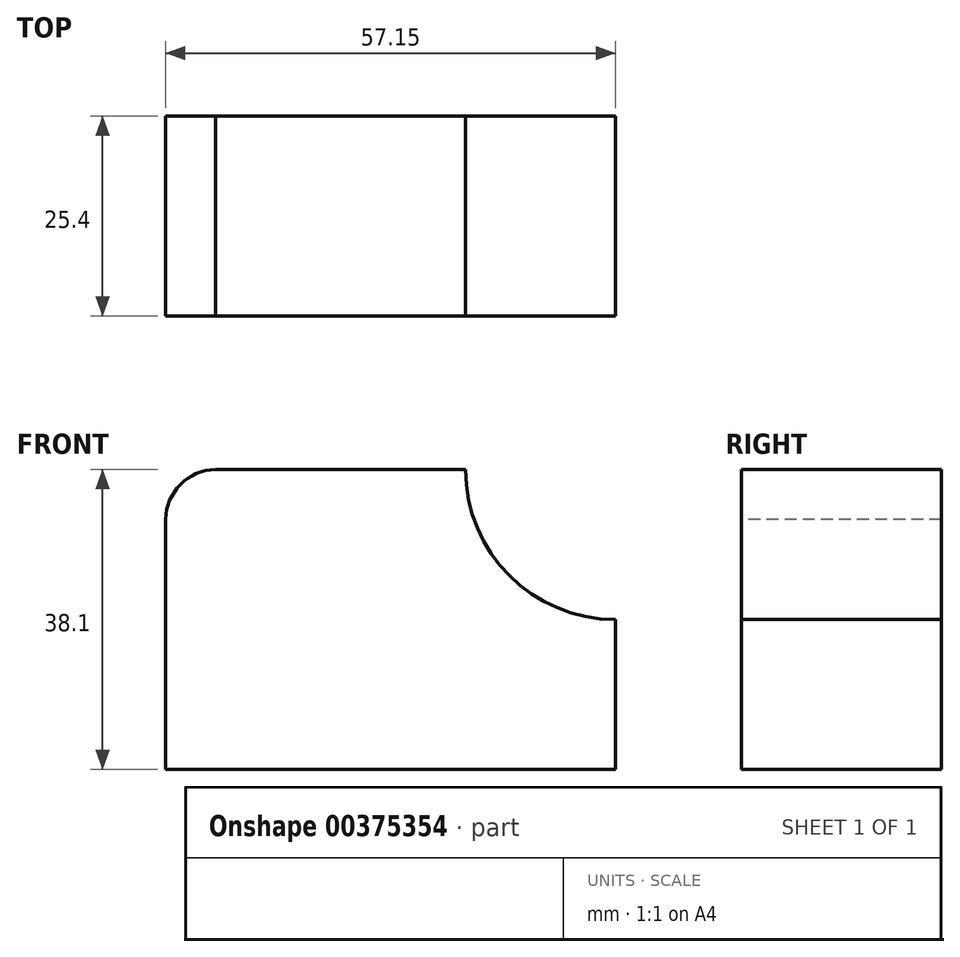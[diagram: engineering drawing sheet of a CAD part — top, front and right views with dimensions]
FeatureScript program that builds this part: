
annotation { "Feature Type Name" : "Feature", "Feature Type Description" : "" }
export const myFeature = defineFeature(function(context is Context, id is Id, definition is map)
    precondition{}
    {
        {
            var Q0;
            Q0=qCreatedBy(makeId("Front.planeOp"),FACE);
            var sketch = newSketch(context, id + "F0", { "sketchPlane" : qUnion([Q0])});
            skLineSegment(sketch, "E0", {"start": v(-35.66, 0) * mm, "end": v(-35.66, 38.1) * mm});
            skLineSegment(sketch, "E1", {"start": v(-35.66, 0) * mm, "end": v(21.49, 0) * mm});
            skLineSegment(sketch, "E2", {"start": v(-35.66, 38.1) * mm, "end": v(21.49, 38.1) * mm});
            skLineSegment(sketch, "E3", {"start": v(21.49, 38.1) * mm, "end": v(21.49, 0) * mm});
            skSolve(sketch);
        }
        {
            var Q0;
            Q0=makeQuery(id+"F0.imprint","IMPRINT",FACE,{"disambiguationData":[TD([[makeQuery(id+"F0.imprint","IMPRINT",EDGE,{"derivedFrom":sQuery(id+"F0.wireOp",EDGE,"E0")}),-1.0]])]});
            extrude(context, id + "F1", {"entities" : qUnion([Q0]), "depth" : 25.4 * mm});
        }
        {
            var Q0;
            Q0=makeQuery(id+"F1.opExtrude","CAP_FACE",FACE,{"disambiguationData":[OSD([sQuery(id+"F0.wireOp",EDGE,"E0"),sQuery(id+"F0.wireOp",EDGE,"E1"),sQuery(id+"F0.wireOp",EDGE,"E2"),sQuery(id+"F0.wireOp",EDGE,"E3")])],"isStart":false});
            var sketch = newSketch(context, id + "F2", { "sketchPlane" : qUnion([Q0])});
            skArc(sketch, "E4", {"start": v(2.44, 38.1) * mm, "mid": v(8.02, 24.63) * mm, "end": v(21.49, 19.05) * mm});
            skArc(sketch, "E5", {"start": v(-22.96, 38.1) * mm, "mid": v(-35.66, 38.1) * mm, "end": v(-35.66, 25.4) * mm});
            skSolve(sketch);
        }
        {
            var Q0;
            {var subQ0=sQuery(id+"F2.wireOp",EDGE,"E4");Q0=makeQuery(id+"F2.imprint","IMPRINT",FACE,{"disambiguationData":[TD([[makeQuery(id+"F2.imprint","IMPRINT",EDGE,{"derivedFrom":subQ0}),1.0]])]});}
            extrude(context, id + "F3", {"entities" : qUnion([Q0]), "operationType" : NewBodyOperationType.REMOVE, "oppositeDirection" : true, "depth" : 25.4 * mm});
        }
        {
            var Q0;
            Q0=makeQuery(id+"F1.opExtrude","CAP_FACE",FACE,{"disambiguationData":[OSD([sQuery(id+"F0.wireOp",EDGE,"E0"),sQuery(id+"F0.wireOp",EDGE,"E1"),sQuery(id+"F0.wireOp",EDGE,"E2"),sQuery(id+"F0.wireOp",EDGE,"E3")])],"isStart":false});
            var sketch = newSketch(context, id + "F4", { "sketchPlane" : qUnion([Q0])});
            skArc(sketch, "E6", {"start": v(-29.31, 38.1) * mm, "mid": v(-33.77, 36.21) * mm, "end": v(-35.66, 31.75) * mm});
            skSolve(sketch);
        }
        {
            var Q0;
            {var subQ0=sQuery(id+"F4.wireOp",EDGE,"E6");Q0=makeQuery(id+"F4.imprint","IMPRINT",FACE,{"disambiguationData":[TD([[makeQuery(id+"F4.imprint","IMPRINT",EDGE,{"derivedFrom":subQ0}),-1.0]])]});}
            extrude(context, id + "F5", {"entities" : qUnion([Q0]), "operationType" : NewBodyOperationType.REMOVE, "oppositeDirection" : true, "depth" : 25.4 * mm});
        }
    });
